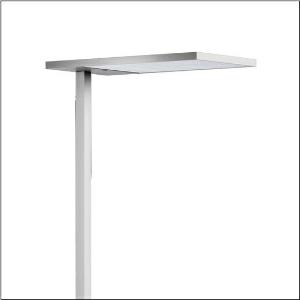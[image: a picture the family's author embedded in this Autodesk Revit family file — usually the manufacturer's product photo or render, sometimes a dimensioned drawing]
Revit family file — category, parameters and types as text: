
# Revit family: silica_r__21_floor_r_51mx53sg4ds_70f9
name_source: partatom
category: Lighting Fixtures
units: mm (PartAtom-declared; Revit-internal decimal feet)

## family parameters
Cut with Voids When Loaded = No
Host = Face
Light Source = No
Part Type = Normal
Room Calculation Point = No
Round Connector Dimension = Use Diameter
Shared = No

## types (1)
- Silica® 21 Floor R (1 x LED, 15000 lm, 106.4 W, 4000K)
    Apparent Load = 106 VA
    CIE Flux Codes = 54 86 97 13 100
    Color Rendering = 80
    Color Temperature = 4000K
    Default Elevation = 1800 mm
    Description = Silica® 21 Floor R, floorstanding luminaire, of PMMA, primary optical cover: prismatic diffuser, of PMMA, CAT 2 (L<= 3000cd/m²), light emission: indirect/direct distribution, primary light characteristic: symmetric, installation type: not mounted, LED, rated luminous flux: 15.000lm, luminous efficacy: 141lm/W, light colour: 840, colour temperature: 4000K, control gear: ECG DALI, daylight-dependent control, mains connection: 230V, 50Hz, connection cable pre-assembled, cable length: 2,5m, rated input power: 106.4W, luminaire head, of aluminium, metallic grey (RAL 9006), length: 650mm, width: 350mm, supporting column, angular, of aluminium, metallic grey (RAL 9006), baseplate, of steel, metallic grey (RAL 9006), protection rating (complete): IP20, insulation class (complete): insulation class I (protective earthing), certification: CE, standard: EN 50419, packaging unit: 1 piece
    Height = 18 mm
    Lamp = 1 x LED
    Lamp Light Flux = 15000 lm
    Lamp Power = 106.4 W
    Lamp count = 1
    Length = 650 mm
    Luminous efficacy = 141 lm/W
    Manufacturer = Siteco
    ModVariant = No
    Model = 51MX53SG4DS
    Mounting Place = Floor
    Mounting Type = Freestanding
    Number of Poles = 1
    OnlyDefault = Yes
    Power Factor = 1
    Product Name = Silica® 21 Floor R
    Product group = floorstanding luminaire
    ProductGroupID = 1301
    Protection Class = Protection class I
    Protection Degree = IP 20
    RLX_Detail_Level = 1
    RLX_Emergency_Light_Flux = 0 lm
    RLX_Emergency_Type = 0
    RLX_Emergency_Type_DB = No
    RlxData = <blob elided: 20177 chars, md5=a906b1f1>
    Socket = socket
    Standby Power = 0 W
    System Light Flux = 15000 lm
    System Power = 106 W
    Type Comments = Product without accessories
    Type Image = l_1006716.jpg
    URL = http://relux.com
    VarID = ---
    Voltage = 0 V
    Weight = 0.00 kg
    Width = 350 mm

## geometry (parser evidence)
native form markers: Blend x4, Sweep x15
no freeform markers — native parametric forms only
